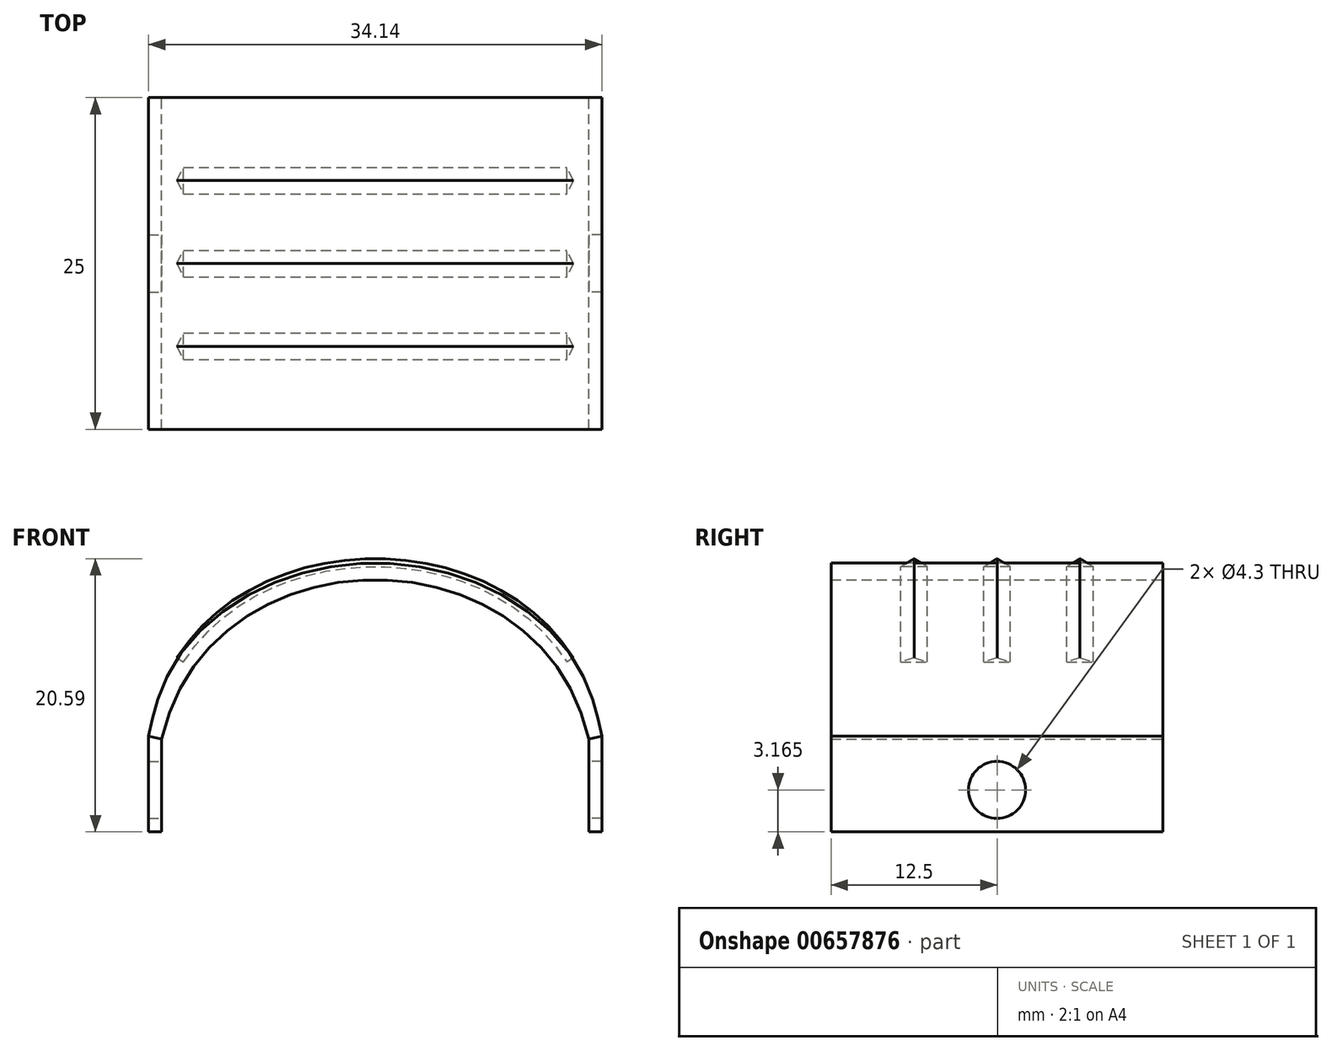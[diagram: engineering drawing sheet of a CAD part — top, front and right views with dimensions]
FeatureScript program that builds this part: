
annotation { "Feature Type Name" : "Feature", "Feature Type Description" : "" }
export const myFeature = defineFeature(function(context is Context, id is Id, definition is map)
    precondition{}
    {
        {
            var Q0;
            Q0=qCreatedBy(makeId("Front.planeOp"),FACE);
            var sketch = newSketch(context, id + "F0", { "sketchPlane" : qUnion([Q0])});
            skFitSpline(sketch, "E0", {"points": [v(-16.1, 0) * mm, v(16.1, 0) * mm], "startDerivative": vector(10.87, 47.99) * mm, "endDerivative": vector(10.87, -47.99) * mm});
            skFitSpline(sketch, "E1.0", {"points": [v(-17.07, 0.22) * mm, v(-16.6, 2.34) * mm, v(-14.91, 6.09) * mm, v(-10.79, 10.1) * mm, v(-5.64, 12.47) * mm, v(0, 13.26) * mm, v(5.64, 12.47) * mm, v(10.79, 10.1) * mm, v(14.91, 6.09) * mm, v(16.6, 2.34) * mm, v(17.07, 0.22) * mm]});
            skLineSegment(sketch, "E2", {"start": v(-16.1, 0) * mm, "end": v(-17.07, 0.22) * mm});
            skLineSegment(sketch, "E3", {"start": v(16.1, 0) * mm, "end": v(17.07, 0.22) * mm});
            skSolve(sketch);
        }
        {
            var Q0;
            Q0 = qSketchRegion(id + "F0", true);
            extrude(context, id + "F1", {"entities" : qUnion([Q0]), "depth" : 25 * mm, "offsetDistance" : 25 * mm, "symmetric" : true});
        }
        {
            var Q0;
            Q0=qCreatedBy(makeId("Right.planeOp"),FACE);
            var sketch = newSketch(context, id + "F2", { "sketchPlane" : qUnion([Q0])});
            skLineSegment(sketch, "E4", {"start": v(-7.25, 13) * mm, "end": v(-5.25, 13) * mm});
            skLineSegment(sketch, "E5", {"start": v(-6.25, 13.6) * mm, "end": v(-7.25, 13) * mm});
            skLineSegment(sketch, "E6", {"start": v(-6.25, 13.6) * mm, "end": v(-5.25, 13) * mm});
            skLineSegment(sketch, "E7", {"start": v(-6.25, 13.6) * mm, "end": v(-6.25, 13) * mm});
            skLineSegment(sketch, "E8", {"start": v(-1, 13) * mm, "end": v(1, 13) * mm});
            skLineSegment(sketch, "E9", {"start": v(0, 13.6) * mm, "end": v(-1, 13) * mm});
            skLineSegment(sketch, "E10", {"start": v(0, 13.6) * mm, "end": v(1, 13) * mm});
            skLineSegment(sketch, "E11", {"start": v(0, 13.6) * mm, "end": v(0, 13) * mm});
            skLineSegment(sketch, "E12", {"start": v(5.25, 13) * mm, "end": v(7.25, 13) * mm});
            skLineSegment(sketch, "E13", {"start": v(6.25, 13.6) * mm, "end": v(5.25, 13) * mm});
            skLineSegment(sketch, "E14", {"start": v(6.25, 13.6) * mm, "end": v(7.25, 13) * mm});
            skLineSegment(sketch, "E15", {"start": v(6.25, 13.6) * mm, "end": v(6.25, 13) * mm});
            skSolve(sketch);
        }
        {
            var Q0;
            Q0=qCreatedBy(makeId("Front.planeOp"),FACE);
            var sketch = newSketch(context, id + "F3", { "sketchPlane" : qUnion([Q0])});
            skFitSpline(sketch, "E16", {"points": [v(-14.64, 5.94) * mm, v(14.64, 5.94) * mm], "startDerivative": vector(18.62, 29.2) * mm, "endDerivative": vector(18.62, -29.2) * mm});
            skSolve(sketch);
        }
        {
            var Q0;
            {var subQ0=sQuery(id+"F2.wireOp",EDGE,"E5");Q0=makeQuery(id+"F2.imprint","IMPRINT",FACE,{"disambiguationData":[TD([[makeQuery(id+"F2.imprint","IMPRINT",EDGE,{"derivedFrom":subQ0}),1.0]])]});}
            var Q1;
            {var subQ0=sQuery(id+"F2.wireOp",EDGE,"E6");Q1=makeQuery(id+"F2.imprint","IMPRINT",FACE,{"disambiguationData":[TD([[makeQuery(id+"F2.imprint","IMPRINT",EDGE,{"derivedFrom":subQ0}),-1.0]])]});}
            var Q2;
            {var subQ0=sQuery(id+"F2.wireOp",EDGE,"E9");Q2=makeQuery(id+"F2.imprint","IMPRINT",FACE,{"disambiguationData":[TD([[makeQuery(id+"F2.imprint","IMPRINT",EDGE,{"derivedFrom":subQ0}),1.0]])]});}
            var Q3;
            {var subQ0=sQuery(id+"F2.wireOp",EDGE,"E10");Q3=makeQuery(id+"F2.imprint","IMPRINT",FACE,{"disambiguationData":[TD([[makeQuery(id+"F2.imprint","IMPRINT",EDGE,{"derivedFrom":subQ0}),-1.0]])]});}
            var Q4;
            {var subQ0=sQuery(id+"F2.wireOp",EDGE,"E14");Q4=makeQuery(id+"F2.imprint","IMPRINT",FACE,{"disambiguationData":[TD([[makeQuery(id+"F2.imprint","IMPRINT",EDGE,{"derivedFrom":subQ0}),-1.0]])]});}
            var Q5;
            {var subQ0=sQuery(id+"F2.wireOp",EDGE,"E13");Q5=makeQuery(id+"F2.imprint","IMPRINT",FACE,{"disambiguationData":[TD([[makeQuery(id+"F2.imprint","IMPRINT",EDGE,{"derivedFrom":subQ0}),1.0]])]});}
            var Q6;
            Q6=sQuery(id+"F3.wireOp",EDGE,"E16");
            sweep(context, id + "F4", {"profiles" : qUnion([Q0, Q1, Q2, Q3, Q4, Q5]), "path" : qUnion([Q6])});
        }
        {
            var Q0;
            Q0=qCreatedBy(makeId("Front.planeOp"),FACE);
            var sketch = newSketch(context, id + "F5", { "sketchPlane" : qUnion([Q0])});
            skLineSegment(sketch, "E17", {"start": v(16.1, 0) * mm, "end": v(16.1, -7) * mm});
            skLineSegment(sketch, "E18", {"start": v(17.07, 0.22) * mm, "end": v(17.07, -7) * mm});
            skLineSegment(sketch, "E19", {"start": v(16.1, -7) * mm, "end": v(17.07, -7) * mm});
            skLineSegment(sketch, "E20", {"start": v(16.1, 0) * mm, "end": v(17.07, 0.22) * mm});
            skLineSegment(sketch, "E21.MirrorCS", {"start": v(-16.1, 0) * mm, "end": v(-17.07, 0.22) * mm});
            skLineSegment(sketch, "E22.MirrorCS", {"start": v(-16.1, -7) * mm, "end": v(-17.07, -7) * mm});
            skLineSegment(sketch, "E23.MirrorCS", {"start": v(-16.1, 0) * mm, "end": v(-16.1, -7) * mm});
            skLineSegment(sketch, "E24.MirrorCS", {"start": v(-17.07, 0.22) * mm, "end": v(-17.07, -7) * mm});
            skLineSegment(sketch, "E25", {"start": v(16.1, -7) * mm, "end": v(16.1, -6) * mm});
            skLineSegment(sketch, "E26", {"start": v(16.1, -6) * mm, "end": v(16.1, -3.85) * mm});
            skSolve(sketch);
        }
        {
            var Q0;
            Q0 = qSketchRegion(id + "F5", true);
            extrude(context, id + "F6", {"entities" : qUnion([Q0]), "depth" : 25 * mm, "offsetDistance" : 25 * mm, "symmetric" : true});
        }
        {
            var Q0;
            Q0=qCreatedBy(makeId("Right.planeOp"),FACE);
            var sketch = newSketch(context, id + "F7", { "sketchPlane" : qUnion([Q0])});
            skPoint(sketch, "E27", {"position": v(0, -3.84) * mm});
            skSolve(sketch);
        }
        {
            var Q0;
            Q0=sQuery(id+"F7.wireOp",VERTEX,"E27");
            var Q1;
            Q1=makeQuery(id+"F6.opExtrude","SWEPT_BODY",BODY,{"disambiguationData":[OSD([sQuery(id+"F5.wireOp",EDGE,"E21.MirrorCS"),sQuery(id+"F5.wireOp",EDGE,"E22.MirrorCS"),sQuery(id+"F5.wireOp",EDGE,"E23.MirrorCS"),sQuery(id+"F5.wireOp",EDGE,"E24.MirrorCS")])]});
            var Q2;
            Q2=makeQuery(id+"F6.opExtrude","SWEPT_BODY",BODY,{"disambiguationData":[OSD([sQuery(id+"F5.wireOp",EDGE,"E17"),sQuery(id+"F5.wireOp",EDGE,"E18"),sQuery(id+"F5.wireOp",EDGE,"E19"),sQuery(id+"F5.wireOp",EDGE,"E20"),sQuery(id+"F5.wireOp",EDGE,"E25"),sQuery(id+"F5.wireOp",EDGE,"E26")])]});
            hole(context, id + "F8", {"style" : HoleStyle.SIMPLE, "endStyle" : HoleEndStyle.THROUGH, "holeDiameter" : 4.3 * mm, "majorDiameter" : 5 * mm, "isTappedThrough" : true, "tappedDepth" : 12 * mm, "tapClearance" : 3, "locations" : qUnion([Q0]), "scope" : qUnion([Q1, Q2])});
        }
        {
            var Q0;
            Q0=sQuery(id+"F7.wireOp",VERTEX,"E27");
            var Q1;
            Q1=makeQuery(id+"F6.opExtrude","SWEPT_BODY",BODY,{"disambiguationData":[OSD([sQuery(id+"F5.wireOp",EDGE,"E17"),sQuery(id+"F5.wireOp",EDGE,"E18"),sQuery(id+"F5.wireOp",EDGE,"E19"),sQuery(id+"F5.wireOp",EDGE,"E20"),sQuery(id+"F5.wireOp",EDGE,"E25"),sQuery(id+"F5.wireOp",EDGE,"E26")])]});
            hole(context, id + "F9", {"style" : HoleStyle.SIMPLE, "endStyle" : HoleEndStyle.THROUGH, "oppositeDirection" : true, "holeDiameter" : 4.3 * mm, "majorDiameter" : 5 * mm, "isTappedThrough" : true, "tappedDepth" : 12 * mm, "tapClearance" : 3, "locations" : qUnion([Q0]), "scope" : qUnion([Q1])});
        }
    });
